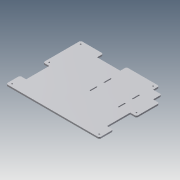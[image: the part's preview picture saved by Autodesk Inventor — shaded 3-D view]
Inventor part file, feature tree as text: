
AUTODESK INVENTOR PART (.ipt)
format: ipt  version: 2014 (Build 180170000, 170)  size: 219,648 bytes
history: native  units: mm
features: extrude x5, sketch x5, fillet x1
ambient origin geometry x8: Origin, YZ Plane, XZ Plane, XY Plane, X Axis, Y Axis, Z Axis, Center Point
bodies: Solid1 (feature_tree)
feature tree (11):
  extrude  "Extrusion1"  Depth=300.0mm
  extrude  "Extrusion6"  Depth=25.0mm
  extrude  "Extrusion7"  Depth=160.0mm
  extrude  "Extrusion8"  Depth=4.0mm TaperAngle=0.0deg
  extrude  "Extrusion9"  Depth=34.0mm
  fillet  "Fillet3"  Radius=12.5mm
  sketch  "Sketch1"  dims[d0=375.0mm d1=300.0mm]
  sketch  "Sketch6"  dims[d2=6.0mm d3=0.0mm d22=25.0mm]
  sketch  "Sketch7"  dims[d23=4.0mm d24=0.0mm d25=160.0mm]
  sketch  "Sketch8"  dims[d26=200.0mm d28=4.0mm d29=0.0mm]
  sketch  "Sketch9"  dims[d30=6.0mm d31=34.0mm d32=12.5mm d33=12.5mm d34=12.5mm d35=12.5mm d36=12.5mm d37=5.4mm d38=10.0mm d39=0.0mm d40=114.0mm d41=2.15mm d42=56.6mm d43=25.0mm d44=85.0mm d45=10.0mm d46=0.0mm]
